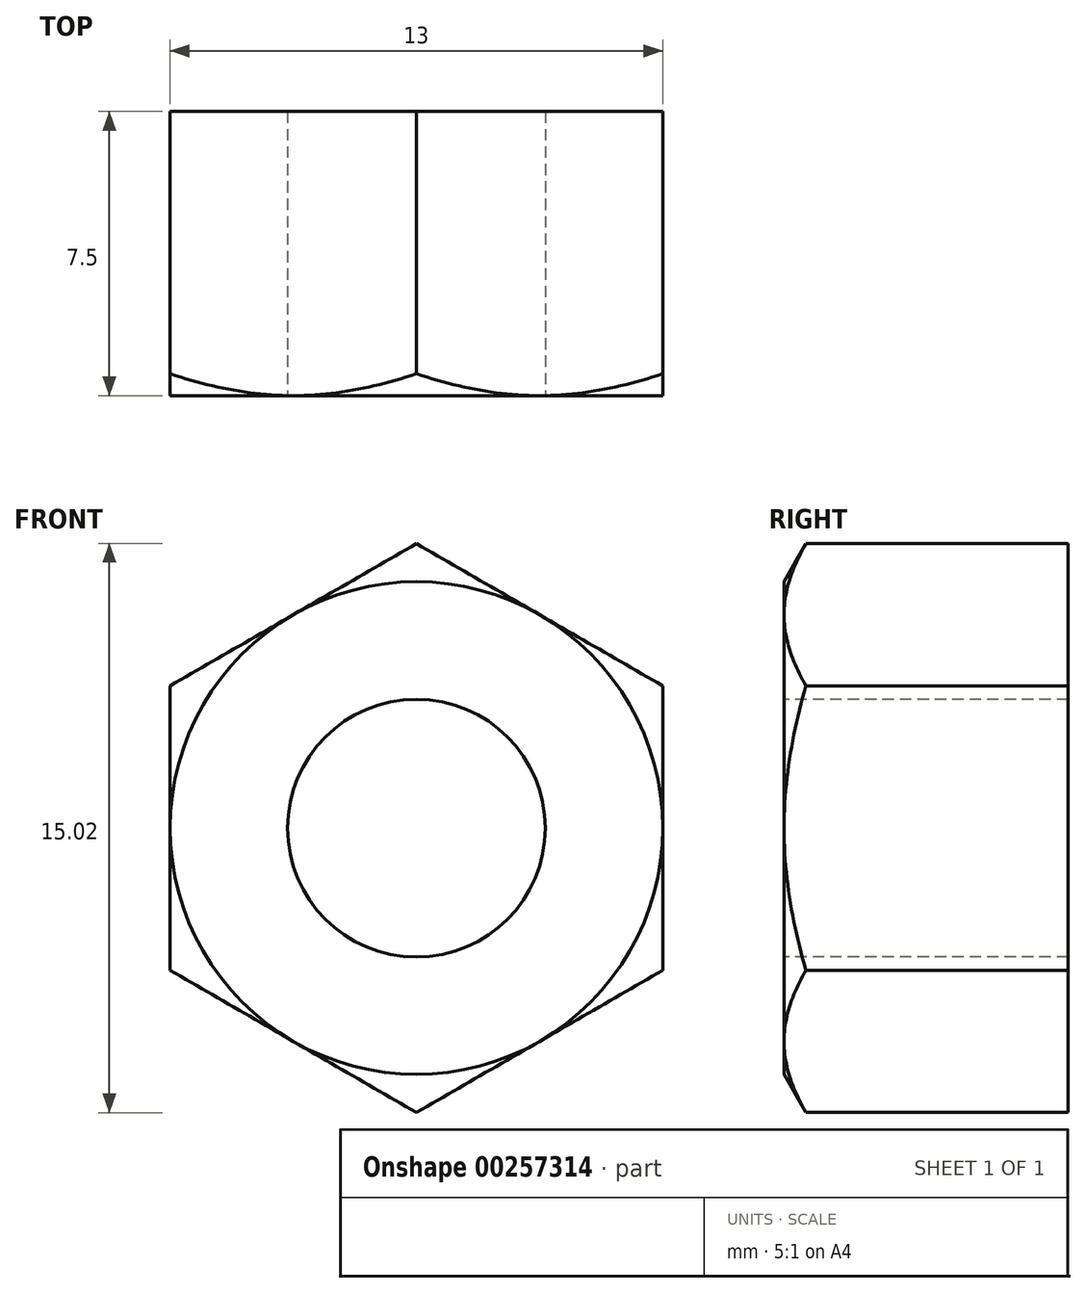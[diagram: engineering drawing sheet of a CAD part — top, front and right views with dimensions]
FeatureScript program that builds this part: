
annotation { "Feature Type Name" : "Feature", "Feature Type Description" : "" }
export const myFeature = defineFeature(function(context is Context, id is Id, definition is map)
    precondition{}
    {
        {
            var Q0;
            Q0=qCreatedBy(makeId("Front.planeOp"),FACE);
            var sketch = newSketch(context, id + "F0", { "sketchPlane" : qUnion([Q0])});
            skCircle(sketch, "E0.cCircle", {"center": v(0, 0) * mm, "radius": 6.5 * mm, "construction": true});
            skLineSegment(sketch, "E0.0", {"start": v(6.5, 3.75) * mm, "end": v(6.5, -3.75) * mm});
            skLineSegment(sketch, "E0.1", {"start": v(6.5, -3.75) * mm, "end": v(0, -7.5) * mm});
            skLineSegment(sketch, "E0.2", {"start": v(0, -7.5) * mm, "end": v(-6.5, -3.75) * mm});
            skLineSegment(sketch, "E0.3", {"start": v(-6.5, -3.75) * mm, "end": v(-6.5, 3.75) * mm});
            skLineSegment(sketch, "E0.4", {"start": v(-6.5, 3.75) * mm, "end": v(0, 7.5) * mm});
            skLineSegment(sketch, "E0.5", {"start": v(0, 7.5) * mm, "end": v(6.5, 3.75) * mm});
            skPoint(sketch, "E0.0.midPoint", {"position": v(6.5, 0) * mm});
            skSolve(sketch);
        }
        {
            var Q0;
            Q0=makeQuery(id+"F0.imprint","IMPRINT",FACE,{"disambiguationData":[TD([[makeQuery(id+"F0.imprint","IMPRINT",EDGE,{"derivedFrom":sQuery(id+"F0.wireOp",EDGE,"E0.0")}),-1.0]])]});
            extrude(context, id + "F1", {"entities" : qUnion([Q0]), "oppositeDirection" : true, "depth" : 7.5 * mm});
        }
        {
            var Q0;
            Q0=qCreatedBy(makeId("Right.planeOp"),FACE);
            var sketch = newSketch(context, id + "F2", { "sketchPlane" : qUnion([Q0])});
            skLineSegment(sketch, "E1", {"start": v(0, 6.5) * mm, "end": v(2.89, 11.5) * mm});
            skLineSegment(sketch, "E2", {"start": v(2.89, 11.5) * mm, "end": v(0, 11.5) * mm});
            skLineSegment(sketch, "E3", {"start": v(0, 11.5) * mm, "end": v(0, 6.5) * mm});
            skLineSegment(sketch, "E4", {"start": v(-5.97, 0) * mm, "end": v(11.57, 0) * mm, "construction": true});
            skSolve(sketch);
        }
        {
            var Q0;
            Q0=qSketchRegion(id+"F2",true);
            var Q1;
            Q1=sQuery(id+"F2.wireOp",EDGE,"E4");
            revolve(context, id + "F3", {"operationType" : NewBodyOperationType.REMOVE, "entities" : qUnion([Q0]), "axis" : qUnion([Q1]), "revolveType" : RevolveType.FULL, "oppositeDirection" : true});
        }
        {
            var Q0;
            Q0=makeQuery(id+"F1.opExtrude","CAP_FACE",FACE,{"disambiguationData":[OSD([sQuery(id+"F0.wireOp",EDGE,"E0.0"),sQuery(id+"F0.wireOp",EDGE,"E0.1"),sQuery(id+"F0.wireOp",EDGE,"E0.2"),sQuery(id+"F0.wireOp",EDGE,"E0.3"),sQuery(id+"F0.wireOp",EDGE,"E0.4"),sQuery(id+"F0.wireOp",EDGE,"E0.5")])],"isStart":true});
            var sketch = newSketch(context, id + "F4", { "sketchPlane" : qUnion([Q0])});
            skPoint(sketch, "E5", {"position": v(0, 0) * mm});
            skSolve(sketch);
        }
        {
            var Q0;
            Q0=sQuery(id+"F4.wireOp",VERTEX,"E5");
            var Q1;
            Q1=makeQuery(id+"F1.opExtrude","SWEPT_BODY",BODY,{"disambiguationData":[OSD([sQuery(id+"F0.wireOp",EDGE,"E0.0"),sQuery(id+"F0.wireOp",EDGE,"E0.1"),sQuery(id+"F0.wireOp",EDGE,"E0.2"),sQuery(id+"F0.wireOp",EDGE,"E0.3"),sQuery(id+"F0.wireOp",EDGE,"E0.4"),sQuery(id+"F0.wireOp",EDGE,"E0.5")])]});
            hole(context, id + "F5", {"style" : HoleStyle.SIMPLE, "endStyle" : HoleEndStyle.THROUGH, "standardTappedOrClearance" : lookupTablePath({ "standard" : "ISO", "fit" : "Normal", "engagement" : "75%", "pitch" : "1.25 mm", "size" : "M8", "type" : "Tapped" }), "standardBlindInLast" : lookupTablePath({ "fit" : "Standard", "standard" : "ISO", "engagement" : "75%", "pitch" : "1.25 mm", "size" : "M8", "type" : "Tapped" }), "holeDiameter" : 6.8 * mm, "showTappedDepth" : true, "tappedDepth" : 12 * mm, "tapClearance" : 3, "locations" : qUnion([Q0]), "scope" : qUnion([Q1]), "majorDiameter" : 8 * mm});
        }
    });
